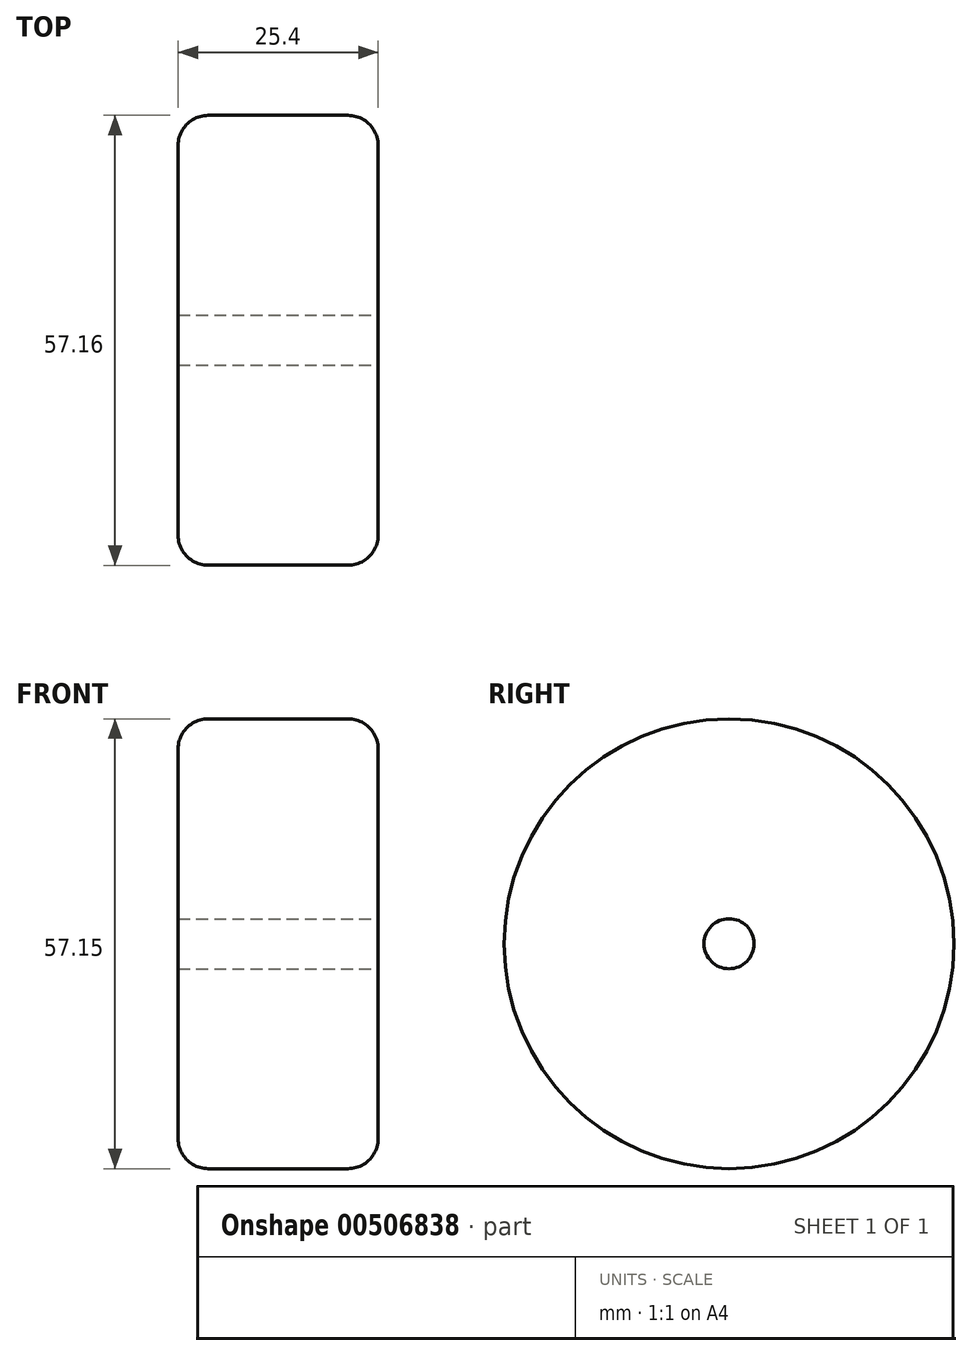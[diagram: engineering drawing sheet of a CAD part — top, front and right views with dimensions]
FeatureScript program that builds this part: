
annotation { "Feature Type Name" : "Feature", "Feature Type Description" : "" }
export const myFeature = defineFeature(function(context is Context, id is Id, definition is map)
    precondition{}
    {
        {
            var Q0;
            Q0=qCreatedBy(makeId("Front.planeOp"),FACE);
            var sketch = newSketch(context, id + "F0", { "sketchPlane" : qUnion([Q0])});
            skLineSegment(sketch, "E0.bottom", {"start": v(-11.98, 12.48) * mm, "end": v(5.8, 12.48) * mm});
            skLineSegment(sketch, "E0.top", {"start": v(-15.8, -16.1) * mm, "end": v(9.6, -16.1) * mm});
            skLineSegment(sketch, "E0.left", {"start": v(-15.8, 8.67) * mm, "end": v(-15.8, -16.1) * mm});
            skLineSegment(sketch, "E0.right", {"start": v(9.6, 8.67) * mm, "end": v(9.6, -16.1) * mm});
            skPoint(sketch, "E1.visualSharp", {"position": v(-15.8, 12.48) * mm});
            skArc(sketch, "E1.filletArc", {"start": v(-11.98, 12.48) * mm, "mid": v(-14.68, 11.37) * mm, "end": v(-15.8, 8.67) * mm});
            skPoint(sketch, "E2.visualSharp", {"position": v(9.6, 12.48) * mm});
            skArc(sketch, "E2.filletArc", {"start": v(9.6, 8.67) * mm, "mid": v(8.5, 11.37) * mm, "end": v(5.8, 12.48) * mm});
            skLineSegment(sketch, "E3", {"start": v(-29.93, -16.1) * mm, "end": v(45.57, -16.1) * mm, "construction": true});
            skSolve(sketch);
        }
        {
            var Q0;
            Q0=makeQuery(id+"F0.imprint","IMPRINT",FACE,{"disambiguationData":[TD([[makeQuery(id+"F0.imprint","IMPRINT",EDGE,{"derivedFrom":sQuery(id+"F0.wireOp",EDGE,"E0.bottom")}),-1.0]])]});
            var Q1;
            Q1=sQuery(id+"F0.wireOp",EDGE,"E3");
            revolve(context, id + "F1", {"surfaceOperationType" : NewSurfaceOperationType.NEW, "entities" : qUnion([Q0]), "axis" : qUnion([Q1]), "revolveType" : RevolveType.FULL});
        }
        {
            var Q0;
            Q0=makeQuery(id+"F1.opRevolve","SWEPT_FACE",FACE,{"disambiguationData":[OSD([sQuery(id+"F0.wireOp",EDGE,"E0.right")])]});
            var sketch = newSketch(context, id + "F2", { "sketchPlane" : qUnion([Q0])});
            skPoint(sketch, "E4", {"position": v(0, -16.1) * mm});
            skSolve(sketch);
        }
        {
            var Q0;
            Q0=sQuery(id+"F2.wireOp",VERTEX,"E4");
            var Q1;
            Q1=makeQuery(id+"F1.opRevolve","SWEPT_BODY",BODY,{"disambiguationData":[OSD([sQuery(id+"F0.wireOp",EDGE,"E0.bottom"),sQuery(id+"F0.wireOp",EDGE,"E0.top"),sQuery(id+"F0.wireOp",EDGE,"E0.left"),sQuery(id+"F0.wireOp",EDGE,"E0.right"),sQuery(id+"F0.wireOp",EDGE,"E1.filletArc"),sQuery(id+"F0.wireOp",EDGE,"E2.filletArc")])]});
            hole(context, id + "F3", {"style" : HoleStyle.SIMPLE, "endStyle" : HoleEndStyle.THROUGH, "holeDiameter" : 6.35 * mm, "majorDiameter" : 6.35 * mm, "isTappedThrough" : true, "tappedDepth" : 12.7 * mm, "tapClearance" : 3, "locations" : qUnion([Q0]), "scope" : qUnion([Q1])});
        }
    });
